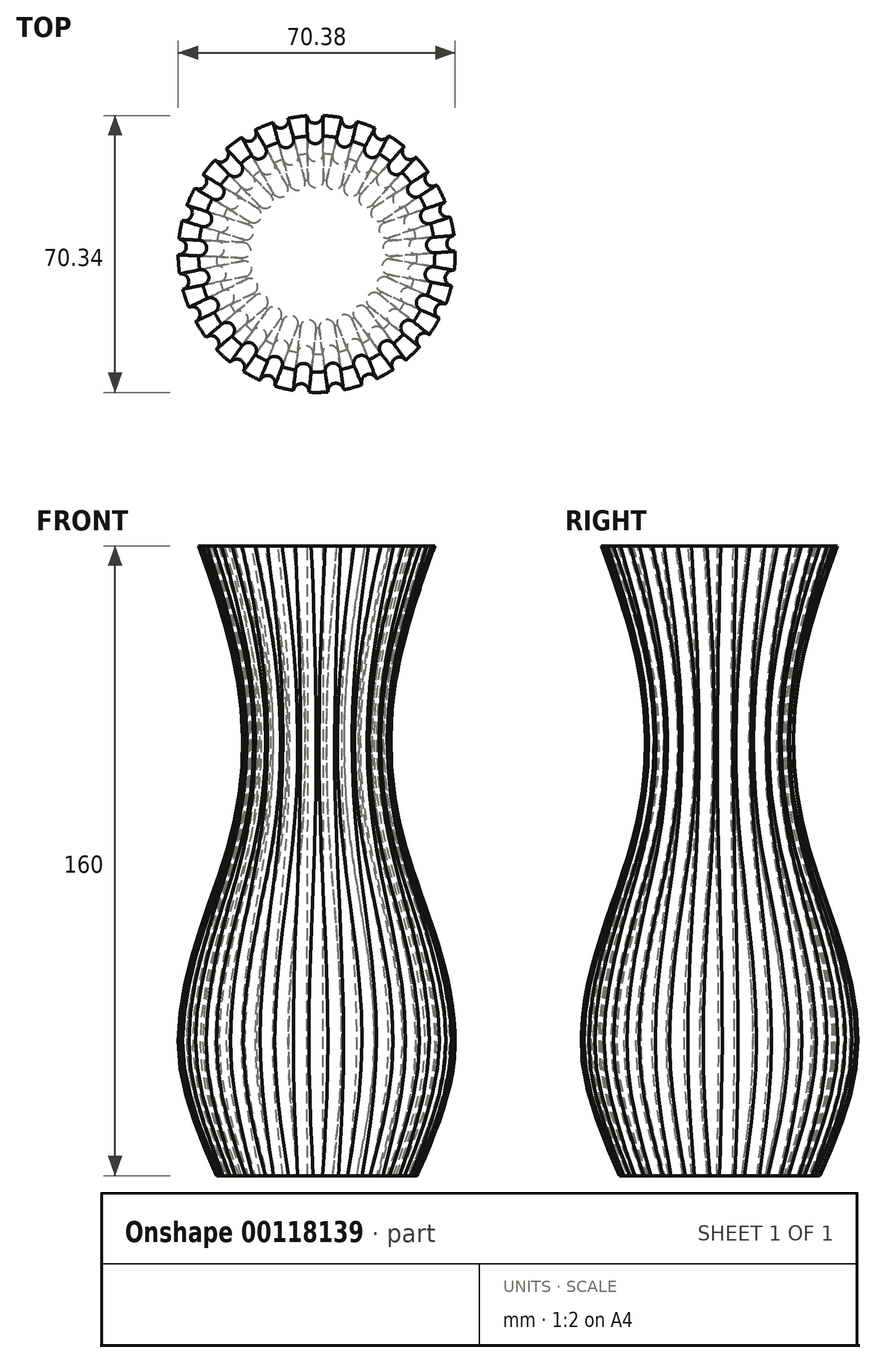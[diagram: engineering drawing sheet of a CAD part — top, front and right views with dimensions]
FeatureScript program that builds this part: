
annotation { "Feature Type Name" : "Feature", "Feature Type Description" : "" }
export const myFeature = defineFeature(function(context is Context, id is Id, definition is map)
    precondition{}
    {
        {
            var Q0;
            Q0=qCreatedBy(makeId("Top.planeOp"),FACE);
            cPlane(context, id + "F0", {"entities" : qUnion([Q0]), "cplaneType" : CPlaneType.OFFSET, "offset" : 30 * mm, "width" : 150 * mm, "height" : 150 * mm});
        }
        {
            var Q0;
            Q0=qCreatedBy(id+"F0.planeOp",FACE);
            cPlane(context, id + "F1", {"entities" : qUnion([Q0]), "cplaneType" : CPlaneType.OFFSET, "offset" : 30 * mm, "width" : 150 * mm, "height" : 150 * mm});
        }
        {
            var Q0;
            Q0=qCreatedBy(id+"F1.planeOp",FACE);
            cPlane(context, id + "F2", {"entities" : qUnion([Q0]), "cplaneType" : CPlaneType.OFFSET, "offset" : 30 * mm, "width" : 150 * mm, "height" : 150 * mm});
        }
        {
            var Q0;
            Q0=qCreatedBy(id+"F2.planeOp",FACE);
            cPlane(context, id + "F3", {"entities" : qUnion([Q0]), "cplaneType" : CPlaneType.OFFSET, "offset" : 35 * mm, "width" : 150 * mm, "height" : 150 * mm});
        }
        {
            var Q0;
            Q0=qCreatedBy(id+"F3.planeOp",FACE);
            cPlane(context, id + "F4", {"entities" : qUnion([Q0]), "cplaneType" : CPlaneType.OFFSET, "offset" : 35 * mm, "width" : 150 * mm, "height" : 150 * mm});
        }
        {
            var Q0;
            Q0=qCreatedBy(id+"F4.planeOp",FACE);
            var sketch = newSketch(context, id + "F5", { "sketchPlane" : qUnion([Q0])});
            skArc(sketch, "E0", {"start": v(-30, -0.5) * mm, "mid": v(-29.91, -2.27) * mm, "end": v(-29.73, -4.02) * mm});
            skArc(sketch, "E1", {"start": v(-29.18, 6.98) * mm, "mid": v(-26.74, 8.31) * mm, "end": v(-28, 10.8) * mm});
            skArc(sketch, "E2.1.0", {"start": v(-30, -0.5) * mm, "mid": v(-27.96, 1.4) * mm, "end": v(-29.8, 3.5) * mm});
            skArc(sketch, "E2.2.0", {"start": v(-28.93, -7.94) * mm, "mid": v(-27.43, -5.6) * mm, "end": v(-29.73, -4.02) * mm});
            skArc(sketch, "E2.3.0", {"start": v(-26.05, -14.89) * mm, "mid": v(-25.18, -12.24) * mm, "end": v(-27.8, -11.3) * mm});
            skArc(sketch, "E2.4.0", {"start": v(-21.53, -20.9) * mm, "mid": v(-21.35, -18.12) * mm, "end": v(-24.11, -17.85) * mm});
            skArc(sketch, "E2.5.0", {"start": v(-15.65, -25.6) * mm, "mid": v(-16.17, -22.86) * mm, "end": v(-18.92, -23.28) * mm});
            skArc(sketch, "E2.6.0", {"start": v(-8.8, -28.68) * mm, "mid": v(-9.97, -26.16) * mm, "end": v(-12.53, -27.26) * mm});
            skArc(sketch, "E2.7.0", {"start": v(-1.39, -29.97) * mm, "mid": v(-3.16, -27.82) * mm, "end": v(-5.36, -29.52) * mm});
            skArc(sketch, "E2.8.0", {"start": v(6.1, -29.37) * mm, "mid": v(3.86, -27.73) * mm, "end": v(2.15, -29.92) * mm});
            skArc(sketch, "E2.9.0", {"start": v(13.22, -26.93) * mm, "mid": v(10.64, -25.9) * mm, "end": v(9.52, -28.45) * mm});
            skArc(sketch, "E2.10.0", {"start": v(19.5, -22.8) * mm, "mid": v(16.75, -22.44) * mm, "end": v(16.3, -25.19) * mm});
            skArc(sketch, "E2.11.0", {"start": v(24.56, -17.23) * mm, "mid": v(21.8, -17.57) * mm, "end": v(22.05, -20.34) * mm});
            skArc(sketch, "E2.12.0", {"start": v(28.07, -10.58) * mm, "mid": v(25.49, -11.6) * mm, "end": v(26.42, -14.22) * mm});
            skArc(sketch, "E2.13.0", {"start": v(29.82, -3.27) * mm, "mid": v(27.57, -4.9) * mm, "end": v(29.12, -7.2) * mm});
            skArc(sketch, "E2.14.0", {"start": v(29.7, 4.25) * mm, "mid": v(27.92, 2.11) * mm, "end": v(30, 0.27) * mm});
            skArc(sketch, "E2.15.0", {"start": v(27.7, 11.5) * mm, "mid": v(26.52, 9) * mm, "end": v(28.99, 7.72) * mm});
            skArc(sketch, "E2.16.0", {"start": v(23.97, 18.03) * mm, "mid": v(23.45, 15.3) * mm, "end": v(26.16, 14.69) * mm});
            skArc(sketch, "E2.17.0", {"start": v(18.74, 23.43) * mm, "mid": v(18.9, 20.65) * mm, "end": v(21.69, 20.73) * mm});
            skArc(sketch, "E2.18.0", {"start": v(12.32, 27.35) * mm, "mid": v(13.18, 24.7) * mm, "end": v(15.85, 25.47) * mm});
            skArc(sketch, "E2.19.0", {"start": v(5.13, 29.56) * mm, "mid": v(6.62, 27.2) * mm, "end": v(9.02, 28.61) * mm});
            skArc(sketch, "E2.20.0", {"start": v(-2.38, 29.9) * mm, "mid": v(-0.36, 28) * mm, "end": v(1.62, 29.96) * mm});
            skArc(sketch, "E2.21.0", {"start": v(-9.74, 28.37) * mm, "mid": v(-7.3, 27.03) * mm, "end": v(-5.88, 29.42) * mm});
            skArc(sketch, "E2.22.0", {"start": v(-16.5, 25.06) * mm, "mid": v(-13.8, 24.36) * mm, "end": v(-13.01, 27.03) * mm});
            skArc(sketch, "E2.23.0", {"start": v(-22.2, 20.17) * mm, "mid": v(-19.43, 20.17) * mm, "end": v(-19.33, 22.94) * mm});
            skArc(sketch, "E2.24.0", {"start": v(-26.53, 14.01) * mm, "mid": v(-23.83, 14.7) * mm, "end": v(-24.43, 17.42) * mm});
            skArc(sketch, "E3.trimOffspring", {"start": v(-28.93, -7.94) * mm, "mid": v(-28.41, -9.63) * mm, "end": v(-27.8, -11.3) * mm});
            skArc(sketch, "E4.trimOffspring", {"start": v(-26.05, -14.89) * mm, "mid": v(-25.12, -16.4) * mm, "end": v(-24.11, -17.85) * mm});
            skArc(sketch, "E5.trimOffspring", {"start": v(-21.53, -20.9) * mm, "mid": v(-20.26, -22.13) * mm, "end": v(-18.92, -23.28) * mm});
            skArc(sketch, "E6.trimOffspring", {"start": v(-15.65, -25.6) * mm, "mid": v(-14.12, -26.47) * mm, "end": v(-12.53, -27.26) * mm});
            skArc(sketch, "E7.trimOffspring", {"start": v(-8.8, -28.68) * mm, "mid": v(-7.09, -29.15) * mm, "end": v(-5.36, -29.52) * mm});
            skArc(sketch, "E8.trimOffspring", {"start": v(-1.39, -29.97) * mm, "mid": v(0.38, -30) * mm, "end": v(2.15, -29.92) * mm});
            skArc(sketch, "E9.trimOffspring", {"start": v(6.1, -29.37) * mm, "mid": v(7.83, -28.96) * mm, "end": v(9.52, -28.45) * mm});
            skArc(sketch, "E10.trimOffspring", {"start": v(13.22, -26.93) * mm, "mid": v(14.79, -26.1) * mm, "end": v(16.3, -25.19) * mm});
            skArc(sketch, "E11.trimOffspring", {"start": v(19.5, -22.8) * mm, "mid": v(20.81, -21.6) * mm, "end": v(22.05, -20.34) * mm});
            skArc(sketch, "E12.trimOffspring", {"start": v(24.56, -17.23) * mm, "mid": v(25.53, -15.75) * mm, "end": v(26.42, -14.22) * mm});
            skArc(sketch, "E13.trimOffspring", {"start": v(28.07, -10.58) * mm, "mid": v(28.65, -8.9) * mm, "end": v(29.12, -7.2) * mm});
            skArc(sketch, "E14.trimOffspring", {"start": v(29.82, -3.27) * mm, "mid": v(29.96, -1.5) * mm, "end": v(30, 0.27) * mm});
            skArc(sketch, "E15.trimOffspring", {"start": v(29.7, 4.25) * mm, "mid": v(29.4, 6) * mm, "end": v(28.99, 7.72) * mm});
            skArc(sketch, "E16.trimOffspring", {"start": v(27.7, 11.5) * mm, "mid": v(26.98, 13.12) * mm, "end": v(26.16, 14.69) * mm});
            skArc(sketch, "E17.trimOffspring", {"start": v(23.97, 18.03) * mm, "mid": v(22.87, 19.42) * mm, "end": v(21.69, 20.73) * mm});
            skArc(sketch, "E18.trimOffspring", {"start": v(18.74, 23.43) * mm, "mid": v(17.32, 24.5) * mm, "end": v(15.85, 25.47) * mm});
            skArc(sketch, "E19.trimOffspring", {"start": v(12.32, 27.35) * mm, "mid": v(10.69, 28.03) * mm, "end": v(9.02, 28.61) * mm});
            skArc(sketch, "E20.trimOffspring", {"start": v(5.13, 29.56) * mm, "mid": v(3.38, 29.8) * mm, "end": v(1.62, 29.96) * mm});
            skArc(sketch, "E21.trimOffspring", {"start": v(-2.38, 29.9) * mm, "mid": v(-4.14, 29.71) * mm, "end": v(-5.88, 29.42) * mm});
            skArc(sketch, "E22.trimOffspring", {"start": v(-9.74, 28.37) * mm, "mid": v(-11.4, 27.75) * mm, "end": v(-13.01, 27.03) * mm});
            skArc(sketch, "E23.trimOffspring", {"start": v(-16.5, 25.06) * mm, "mid": v(-17.94, 24.04) * mm, "end": v(-19.33, 22.94) * mm});
            skArc(sketch, "E24.trimOffspring", {"start": v(-22.2, 20.17) * mm, "mid": v(-23.36, 18.83) * mm, "end": v(-24.43, 17.42) * mm});
            skArc(sketch, "E25.trimOffspring", {"start": v(-26.53, 14.01) * mm, "mid": v(-27.3, 12.43) * mm, "end": v(-28, 10.8) * mm});
            skArc(sketch, "E26.trimOffspring", {"start": v(-29.18, 6.98) * mm, "mid": v(-29.54, 5.25) * mm, "end": v(-29.8, 3.5) * mm});
            skSolve(sketch);
        }
        {
            var Q0;
            Q0=qCreatedBy(id+"F3.planeOp",FACE);
            var sketch = newSketch(context, id + "F6", { "sketchPlane" : qUnion([Q0])});
            skArc(sketch, "E27", {"start": v(-19.98, -1) * mm, "mid": v(-19.94, -1.51) * mm, "end": v(-19.9, -2.02) * mm});
            skArc(sketch, "E28", {"start": v(-19.6, 4) * mm, "mid": v(-17.19, 5.34) * mm, "end": v(-18.4, 7.82) * mm});
            skArc(sketch, "E29.1.0", {"start": v(-19.98, -1) * mm, "mid": v(-17.98, 0.9) * mm, "end": v(-19.78, 3) * mm});
            skArc(sketch, "E29.2.0", {"start": v(-19.1, -5.93) * mm, "mid": v(-17.64, -3.6) * mm, "end": v(-19.9, -2.02) * mm});
            skArc(sketch, "E29.3.0", {"start": v(-17.02, -10.5) * mm, "mid": v(-16.19, -7.87) * mm, "end": v(-18.77, -6.9) * mm});
            skArc(sketch, "E29.4.0", {"start": v(-13.88, -14.4) * mm, "mid": v(-13.72, -11.65) * mm, "end": v(-16.46, -11.36) * mm});
            skArc(sketch, "E29.5.0", {"start": v(-9.86, -17.4) * mm, "mid": v(-10.4, -14.7) * mm, "end": v(-13.12, -15.1) * mm});
            skArc(sketch, "E29.6.0", {"start": v(-5.22, -19.3) * mm, "mid": v(-6.41, -16.82) * mm, "end": v(-8.96, -17.88) * mm});
            skArc(sketch, "E29.7.0", {"start": v(-0.26, -20) * mm, "mid": v(-2.03, -17.89) * mm, "end": v(-4.23, -19.55) * mm});
            skArc(sketch, "E29.8.0", {"start": v(4.72, -19.43) * mm, "mid": v(2.48, -17.83) * mm, "end": v(0.77, -19.99) * mm});
            skArc(sketch, "E29.9.0", {"start": v(9.4, -17.65) * mm, "mid": v(6.84, -16.65) * mm, "end": v(5.71, -19.17) * mm});
            skArc(sketch, "E29.10.0", {"start": v(13.5, -14.75) * mm, "mid": v(10.76, -14.43) * mm, "end": v(10.3, -17.14) * mm});
            skArc(sketch, "E29.11.0", {"start": v(16.75, -10.93) * mm, "mid": v(14.01, -11.3) * mm, "end": v(14.24, -14.04) * mm});
            skArc(sketch, "E29.12.0", {"start": v(18.94, -6.42) * mm, "mid": v(16.38, -7.46) * mm, "end": v(17.29, -10.06) * mm});
            skArc(sketch, "E29.13.0", {"start": v(19.94, -1.51) * mm, "mid": v(17.72, -3.15) * mm, "end": v(19.24, -5.45) * mm});
            skArc(sketch, "E29.14.0", {"start": v(19.7, 3.5) * mm, "mid": v(17.95, 1.36) * mm, "end": v(20, -0.49) * mm});
            skArc(sketch, "E29.15.0", {"start": v(18.2, 8.28) * mm, "mid": v(17.05, 5.78) * mm, "end": v(19.49, 4.5) * mm});
            skArc(sketch, "E29.16.0", {"start": v(15.57, 12.55) * mm, "mid": v(15.07, 9.84) * mm, "end": v(17.76, 9.2) * mm});
            skArc(sketch, "E29.17.0", {"start": v(11.96, 16.03) * mm, "mid": v(12.15, 13.28) * mm, "end": v(14.9, 13.33) * mm});
            skArc(sketch, "E29.18.0", {"start": v(7.6, 18.5) * mm, "mid": v(8.47, 15.88) * mm, "end": v(11.13, 16.62) * mm});
            skArc(sketch, "E29.19.0", {"start": v(2.76, 19.8) * mm, "mid": v(4.25, 17.5) * mm, "end": v(6.64, 18.86) * mm});
            skArc(sketch, "E29.20.0", {"start": v(-2.25, 19.87) * mm, "mid": v(-0.23, 18) * mm, "end": v(1.74, 19.92) * mm});
            skArc(sketch, "E29.21.0", {"start": v(-7.12, 18.69) * mm, "mid": v(-4.7, 17.38) * mm, "end": v(-3.27, 19.73) * mm});
            skArc(sketch, "E29.22.0", {"start": v(-11.55, 16.33) * mm, "mid": v(-8.87, 15.66) * mm, "end": v(-8.07, 18.3) * mm});
            skArc(sketch, "E29.23.0", {"start": v(-15.24, 12.95) * mm, "mid": v(-12.49, 12.96) * mm, "end": v(-12.37, 15.72) * mm});
            skArc(sketch, "E29.24.0", {"start": v(-17.99, 8.75) * mm, "mid": v(-15.32, 9.45) * mm, "end": v(-15.89, 12.15) * mm});
            skArc(sketch, "E30.trimOffspring", {"start": v(-19.1, -5.93) * mm, "mid": v(-18.94, -6.42) * mm, "end": v(-18.77, -6.9) * mm});
            skArc(sketch, "E31.trimOffspring", {"start": v(-17.02, -10.5) * mm, "mid": v(-16.75, -10.93) * mm, "end": v(-16.46, -11.36) * mm});
            skArc(sketch, "E32.trimOffspring", {"start": v(-13.88, -14.4) * mm, "mid": v(-13.5, -14.75) * mm, "end": v(-13.12, -15.1) * mm});
            skArc(sketch, "E33.trimOffspring", {"start": v(-9.86, -17.4) * mm, "mid": v(-9.41, -17.65) * mm, "end": v(-8.96, -17.88) * mm});
            skArc(sketch, "E34.trimOffspring", {"start": v(-5.22, -19.3) * mm, "mid": v(-4.73, -19.43) * mm, "end": v(-4.23, -19.55) * mm});
            skArc(sketch, "E35.trimOffspring", {"start": v(-0.26, -20) * mm, "mid": v(0.25, -20) * mm, "end": v(0.77, -19.99) * mm});
            skArc(sketch, "E36.trimOffspring", {"start": v(4.72, -19.43) * mm, "mid": v(5.22, -19.3) * mm, "end": v(5.71, -19.17) * mm});
            skArc(sketch, "E37.trimOffspring", {"start": v(9.4, -17.65) * mm, "mid": v(9.86, -17.4) * mm, "end": v(10.3, -17.14) * mm});
            skArc(sketch, "E38.trimOffspring", {"start": v(13.5, -14.75) * mm, "mid": v(13.88, -14.4) * mm, "end": v(14.24, -14.04) * mm});
            skArc(sketch, "E39.trimOffspring", {"start": v(16.75, -10.93) * mm, "mid": v(17.02, -10.5) * mm, "end": v(17.29, -10.06) * mm});
            skArc(sketch, "E40.trimOffspring", {"start": v(18.94, -6.42) * mm, "mid": v(19.1, -5.94) * mm, "end": v(19.24, -5.45) * mm});
            skArc(sketch, "E41.trimOffspring", {"start": v(19.94, -1.51) * mm, "mid": v(19.97, -1) * mm, "end": v(20, -0.49) * mm});
            skArc(sketch, "E42.trimOffspring", {"start": v(19.7, 3.5) * mm, "mid": v(19.6, 4) * mm, "end": v(19.49, 4.5) * mm});
            skArc(sketch, "E43.trimOffspring", {"start": v(18.2, 8.28) * mm, "mid": v(17.99, 8.75) * mm, "end": v(17.76, 9.2) * mm});
            skArc(sketch, "E44.trimOffspring", {"start": v(15.57, 12.55) * mm, "mid": v(15.25, 12.94) * mm, "end": v(14.9, 13.33) * mm});
            skArc(sketch, "E45.trimOffspring", {"start": v(11.96, 16.03) * mm, "mid": v(11.55, 16.33) * mm, "end": v(11.13, 16.62) * mm});
            skArc(sketch, "E46.trimOffspring", {"start": v(7.6, 18.5) * mm, "mid": v(7.12, 18.69) * mm, "end": v(6.64, 18.86) * mm});
            skArc(sketch, "E47.trimOffspring", {"start": v(2.76, 19.8) * mm, "mid": v(2.25, 19.87) * mm, "end": v(1.74, 19.92) * mm});
            skArc(sketch, "E48.trimOffspring", {"start": v(-2.25, 19.87) * mm, "mid": v(-2.76, 19.8) * mm, "end": v(-3.27, 19.73) * mm});
            skArc(sketch, "E49.trimOffspring", {"start": v(-7.12, 18.69) * mm, "mid": v(-7.6, 18.5) * mm, "end": v(-8.07, 18.3) * mm});
            skArc(sketch, "E50.trimOffspring", {"start": v(-11.55, 16.33) * mm, "mid": v(-11.96, 16.03) * mm, "end": v(-12.37, 15.72) * mm});
            skArc(sketch, "E51.trimOffspring", {"start": v(-15.24, 12.95) * mm, "mid": v(-15.57, 12.55) * mm, "end": v(-15.89, 12.15) * mm});
            skArc(sketch, "E52.trimOffspring", {"start": v(-17.99, 8.75) * mm, "mid": v(-18.2, 8.28) * mm, "end": v(-18.4, 7.82) * mm});
            skArc(sketch, "E53.trimOffspring", {"start": v(-19.6, 4) * mm, "mid": v(-19.7, 3.5) * mm, "end": v(-19.78, 3) * mm});
            skSolve(sketch);
        }
        {
            var Q0;
            Q0=qCreatedBy(id+"F2.planeOp",FACE);
            var sketch = newSketch(context, id + "F7", { "sketchPlane" : qUnion([Q0])});
            skArc(sketch, "E54", {"start": v(-20.98, -0.95) * mm, "mid": v(-20.94, -1.59) * mm, "end": v(-20.88, -2.22) * mm});
            skArc(sketch, "E55", {"start": v(-20.56, 4.3) * mm, "mid": v(-18.14, 5.64) * mm, "end": v(-19.37, 8.11) * mm});
            skArc(sketch, "E56.1.0", {"start": v(-20.98, -0.95) * mm, "mid": v(-18.98, 0.95) * mm, "end": v(-20.78, 3.04) * mm});
            skArc(sketch, "E56.2.0", {"start": v(-20.08, -6.14) * mm, "mid": v(-18.62, -3.8) * mm, "end": v(-20.88, -2.22) * mm});
            skArc(sketch, "E56.3.0", {"start": v(-17.93, -10.94) * mm, "mid": v(-17.09, -8.3) * mm, "end": v(-19.67, -7.34) * mm});
            skArc(sketch, "E56.4.0", {"start": v(-14.64, -15.05) * mm, "mid": v(-14.48, -12.3) * mm, "end": v(-17.23, -12) * mm});
            skArc(sketch, "E56.5.0", {"start": v(-10.44, -18.22) * mm, "mid": v(-10.97, -15.51) * mm, "end": v(-13.7, -15.91) * mm});
            skArc(sketch, "E56.6.0", {"start": v(-5.58, -20.24) * mm, "mid": v(-6.77, -17.75) * mm, "end": v(-9.31, -18.82) * mm});
            skArc(sketch, "E56.7.0", {"start": v(-0.37, -21) * mm, "mid": v(-2.14, -18.88) * mm, "end": v(-4.34, -20.55) * mm});
            skArc(sketch, "E56.8.0", {"start": v(4.86, -20.43) * mm, "mid": v(2.62, -18.82) * mm, "end": v(0.9, -20.98) * mm});
            skArc(sketch, "E56.9.0", {"start": v(9.8, -18.58) * mm, "mid": v(7.22, -17.58) * mm, "end": v(6.1, -20.1) * mm});
            skArc(sketch, "E56.10.0", {"start": v(14.1, -15.56) * mm, "mid": v(11.36, -15.23) * mm, "end": v(10.9, -17.95) * mm});
            skArc(sketch, "E56.11.0", {"start": v(17.53, -11.56) * mm, "mid": v(14.8, -11.92) * mm, "end": v(15.02, -14.67) * mm});
            skArc(sketch, "E56.12.0", {"start": v(19.85, -6.84) * mm, "mid": v(17.3, -7.87) * mm, "end": v(18.2, -10.48) * mm});
            skArc(sketch, "E56.13.0", {"start": v(20.93, -1.69) * mm, "mid": v(18.7, -3.32) * mm, "end": v(20.23, -5.62) * mm});
            skArc(sketch, "E56.14.0", {"start": v(20.7, 3.57) * mm, "mid": v(18.95, 1.43) * mm, "end": v(21, -0.41) * mm});
            skArc(sketch, "E56.15.0", {"start": v(19.16, 8.6) * mm, "mid": v(18, 6.1) * mm, "end": v(20.44, 4.82) * mm});
            skArc(sketch, "E56.16.0", {"start": v(16.41, 13.1) * mm, "mid": v(15.91, 10.38) * mm, "end": v(18.6, 9.75) * mm});
            skArc(sketch, "E56.17.0", {"start": v(12.64, 16.77) * mm, "mid": v(12.83, 14.02) * mm, "end": v(15.59, 14.07) * mm});
            skArc(sketch, "E56.18.0", {"start": v(8.07, 19.39) * mm, "mid": v(8.94, 16.77) * mm, "end": v(11.6, 17.5) * mm});
            skArc(sketch, "E56.19.0", {"start": v(3, 20.78) * mm, "mid": v(4.5, 18.46) * mm, "end": v(6.88, 19.84) * mm});
            skArc(sketch, "E56.20.0", {"start": v(-2.26, 20.88) * mm, "mid": v(-0.24, 19) * mm, "end": v(1.73, 20.93) * mm});
            skArc(sketch, "E56.21.0", {"start": v(-7.38, 19.66) * mm, "mid": v(-4.96, 18.34) * mm, "end": v(-3.53, 20.7) * mm});
            skArc(sketch, "E56.22.0", {"start": v(-12.04, 17.2) * mm, "mid": v(-9.36, 16.53) * mm, "end": v(-8.57, 19.17) * mm});
            skArc(sketch, "E56.23.0", {"start": v(-15.94, 13.67) * mm, "mid": v(-13.18, 13.68) * mm, "end": v(-13.06, 16.44) * mm});
            skArc(sketch, "E56.24.0", {"start": v(-18.84, 9.28) * mm, "mid": v(-16.17, 9.98) * mm, "end": v(-16.74, 12.68) * mm});
            skArc(sketch, "E57.trimOffspring", {"start": v(-20.08, -6.14) * mm, "mid": v(-19.89, -6.74) * mm, "end": v(-19.67, -7.34) * mm});
            skArc(sketch, "E58.trimOffspring", {"start": v(-17.93, -10.94) * mm, "mid": v(-17.59, -11.48) * mm, "end": v(-17.23, -12) * mm});
            skArc(sketch, "E59.trimOffspring", {"start": v(-14.64, -15.05) * mm, "mid": v(-14.18, -15.5) * mm, "end": v(-13.7, -15.91) * mm});
            skArc(sketch, "E60.trimOffspring", {"start": v(-10.44, -18.22) * mm, "mid": v(-9.88, -18.53) * mm, "end": v(-9.31, -18.82) * mm});
            skArc(sketch, "E61.trimOffspring", {"start": v(-5.58, -20.24) * mm, "mid": v(-4.96, -20.4) * mm, "end": v(-4.34, -20.55) * mm});
            skArc(sketch, "E62.trimOffspring", {"start": v(-0.37, -21) * mm, "mid": v(0.27, -21) * mm, "end": v(0.9, -20.98) * mm});
            skArc(sketch, "E63.trimOffspring", {"start": v(4.86, -20.43) * mm, "mid": v(5.48, -20.27) * mm, "end": v(6.1, -20.1) * mm});
            skArc(sketch, "E64.trimOffspring", {"start": v(9.8, -18.58) * mm, "mid": v(10.35, -18.27) * mm, "end": v(10.9, -17.95) * mm});
            skArc(sketch, "E65.trimOffspring", {"start": v(14.1, -15.56) * mm, "mid": v(14.57, -15.12) * mm, "end": v(15.02, -14.67) * mm});
            skArc(sketch, "E66.trimOffspring", {"start": v(17.53, -11.56) * mm, "mid": v(17.87, -11.03) * mm, "end": v(18.2, -10.48) * mm});
            skArc(sketch, "E67.trimOffspring", {"start": v(19.85, -6.84) * mm, "mid": v(20.05, -6.23) * mm, "end": v(20.23, -5.62) * mm});
            skArc(sketch, "E68.trimOffspring", {"start": v(20.93, -1.69) * mm, "mid": v(20.97, -1.05) * mm, "end": v(21, -0.41) * mm});
            skArc(sketch, "E69.trimOffspring", {"start": v(20.7, 3.57) * mm, "mid": v(20.58, 4.2) * mm, "end": v(20.44, 4.82) * mm});
            skArc(sketch, "E70.trimOffspring", {"start": v(19.16, 8.6) * mm, "mid": v(18.89, 9.18) * mm, "end": v(18.6, 9.75) * mm});
            skArc(sketch, "E71.trimOffspring", {"start": v(16.41, 13.1) * mm, "mid": v(16, 13.6) * mm, "end": v(15.59, 14.07) * mm});
            skArc(sketch, "E72.trimOffspring", {"start": v(12.64, 16.77) * mm, "mid": v(12.13, 17.15) * mm, "end": v(11.6, 17.5) * mm});
            skArc(sketch, "E73.trimOffspring", {"start": v(8.07, 19.39) * mm, "mid": v(7.48, 19.62) * mm, "end": v(6.88, 19.84) * mm});
            skArc(sketch, "E74.trimOffspring", {"start": v(3, 20.78) * mm, "mid": v(2.37, 20.87) * mm, "end": v(1.73, 20.93) * mm});
            skArc(sketch, "E75.trimOffspring", {"start": v(-2.26, 20.88) * mm, "mid": v(-2.9, 20.8) * mm, "end": v(-3.53, 20.7) * mm});
            skArc(sketch, "E76.trimOffspring", {"start": v(-7.38, 19.66) * mm, "mid": v(-7.98, 19.43) * mm, "end": v(-8.57, 19.17) * mm});
            skArc(sketch, "E77.trimOffspring", {"start": v(-12.04, 17.2) * mm, "mid": v(-12.56, 16.83) * mm, "end": v(-13.06, 16.44) * mm});
            skArc(sketch, "E78.trimOffspring", {"start": v(-15.94, 13.67) * mm, "mid": v(-16.35, 13.18) * mm, "end": v(-16.74, 12.68) * mm});
            skArc(sketch, "E79.trimOffspring", {"start": v(-18.84, 9.28) * mm, "mid": v(-19.11, 8.7) * mm, "end": v(-19.37, 8.11) * mm});
            skArc(sketch, "E80.trimOffspring", {"start": v(-20.56, 4.3) * mm, "mid": v(-20.68, 3.67) * mm, "end": v(-20.78, 3.04) * mm});
            skSolve(sketch);
        }
        {
            var Q0;
            Q0=qCreatedBy(id+"F1.planeOp",FACE);
            var sketch = newSketch(context, id + "F8", { "sketchPlane" : qUnion([Q0])});
            skArc(sketch, "E81", {"start": v(-30.5, -0.47) * mm, "mid": v(-30.41, -2.3) * mm, "end": v(-30.22, -4.12) * mm});
            skArc(sketch, "E82", {"start": v(-29.66, 7.13) * mm, "mid": v(-27.22, 8.46) * mm, "end": v(-28.47, 10.94) * mm});
            skArc(sketch, "E83.1.0", {"start": v(-30.5, -0.47) * mm, "mid": v(-28.46, 1.43) * mm, "end": v(-30.3, 3.52) * mm});
            skArc(sketch, "E83.2.0", {"start": v(-29.42, -8.04) * mm, "mid": v(-27.92, -5.7) * mm, "end": v(-30.22, -4.12) * mm});
            skArc(sketch, "E83.3.0", {"start": v(-26.5, -15.1) * mm, "mid": v(-25.63, -12.46) * mm, "end": v(-28.24, -11.51) * mm});
            skArc(sketch, "E83.4.0", {"start": v(-21.9, -21.22) * mm, "mid": v(-21.73, -18.44) * mm, "end": v(-24.5, -18.17) * mm});
            skArc(sketch, "E83.5.0", {"start": v(-15.94, -26) * mm, "mid": v(-16.46, -23.27) * mm, "end": v(-19.2, -23.7) * mm});
            skArc(sketch, "E83.6.0", {"start": v(-8.97, -29.15) * mm, "mid": v(-10.15, -26.63) * mm, "end": v(-12.7, -27.73) * mm});
            skArc(sketch, "E83.7.0", {"start": v(-1.44, -30.47) * mm, "mid": v(-3.21, -28.32) * mm, "end": v(-5.42, -30.02) * mm});
            skArc(sketch, "E83.8.0", {"start": v(6.18, -29.87) * mm, "mid": v(3.93, -28.23) * mm, "end": v(2.22, -30.42) * mm});
            skArc(sketch, "E83.9.0", {"start": v(13.41, -27.4) * mm, "mid": v(10.83, -26.36) * mm, "end": v(9.71, -28.91) * mm});
            skArc(sketch, "E83.10.0", {"start": v(19.8, -23.2) * mm, "mid": v(17.04, -22.84) * mm, "end": v(16.6, -25.59) * mm});
            skArc(sketch, "E83.11.0", {"start": v(24.95, -17.54) * mm, "mid": v(22.19, -17.89) * mm, "end": v(22.44, -20.66) * mm});
            skArc(sketch, "E83.12.0", {"start": v(28.53, -10.79) * mm, "mid": v(25.94, -11.8) * mm, "end": v(26.87, -14.43) * mm});
            skArc(sketch, "E83.13.0", {"start": v(30.32, -3.35) * mm, "mid": v(28.06, -4.98) * mm, "end": v(29.62, -7.29) * mm});
            skArc(sketch, "E83.14.0", {"start": v(30.2, 4.3) * mm, "mid": v(28.42, 2.15) * mm, "end": v(30.5, 0.3) * mm});
            skArc(sketch, "E83.15.0", {"start": v(28.18, 11.67) * mm, "mid": v(27, 9.15) * mm, "end": v(29.46, 7.88) * mm});
            skArc(sketch, "E83.16.0", {"start": v(24.4, 18.3) * mm, "mid": v(23.87, 15.58) * mm, "end": v(26.58, 14.96) * mm});
            skArc(sketch, "E83.17.0", {"start": v(19.07, 23.8) * mm, "mid": v(19.24, 21.02) * mm, "end": v(22.02, 21.1) * mm});
            skArc(sketch, "E83.18.0", {"start": v(12.56, 27.8) * mm, "mid": v(13.41, 25.15) * mm, "end": v(16.08, 25.91) * mm});
            skArc(sketch, "E83.19.0", {"start": v(5.25, 30.04) * mm, "mid": v(6.74, 27.7) * mm, "end": v(9.13, 29.1) * mm});
            skArc(sketch, "E83.20.0", {"start": v(-2.39, 30.4) * mm, "mid": v(-0.36, 28.5) * mm, "end": v(1.61, 30.46) * mm});
            skArc(sketch, "E83.21.0", {"start": v(-9.87, 28.86) * mm, "mid": v(-7.44, 27.51) * mm, "end": v(-6.01, 29.9) * mm});
            skArc(sketch, "E83.22.0", {"start": v(-16.74, 25.5) * mm, "mid": v(-14.05, 24.8) * mm, "end": v(-13.26, 27.47) * mm});
            skArc(sketch, "E83.23.0", {"start": v(-22.55, 20.53) * mm, "mid": v(-19.77, 20.53) * mm, "end": v(-19.68, 23.3) * mm});
            skArc(sketch, "E83.24.0", {"start": v(-26.95, 14.28) * mm, "mid": v(-24.26, 14.96) * mm, "end": v(-24.85, 17.68) * mm});
            skArc(sketch, "E84.trimOffspring", {"start": v(-29.42, -8.04) * mm, "mid": v(-28.88, -9.8) * mm, "end": v(-28.24, -11.51) * mm});
            skArc(sketch, "E85.trimOffspring", {"start": v(-26.5, -15.1) * mm, "mid": v(-25.54, -16.67) * mm, "end": v(-24.5, -18.17) * mm});
            skArc(sketch, "E86.trimOffspring", {"start": v(-21.9, -21.22) * mm, "mid": v(-20.6, -22.5) * mm, "end": v(-19.2, -23.7) * mm});
            skArc(sketch, "E87.trimOffspring", {"start": v(-15.94, -26) * mm, "mid": v(-14.35, -26.91) * mm, "end": v(-12.7, -27.73) * mm});
            skArc(sketch, "E88.trimOffspring", {"start": v(-8.97, -29.15) * mm, "mid": v(-7.2, -29.64) * mm, "end": v(-5.42, -30.02) * mm});
            skArc(sketch, "E89.trimOffspring", {"start": v(-1.44, -30.47) * mm, "mid": v(0.39, -30.5) * mm, "end": v(2.22, -30.42) * mm});
            skArc(sketch, "E90.trimOffspring", {"start": v(6.18, -29.87) * mm, "mid": v(7.96, -29.44) * mm, "end": v(9.71, -28.91) * mm});
            skArc(sketch, "E91.trimOffspring", {"start": v(13.41, -27.4) * mm, "mid": v(15.03, -26.54) * mm, "end": v(16.6, -25.59) * mm});
            skArc(sketch, "E92.trimOffspring", {"start": v(19.8, -23.2) * mm, "mid": v(21.16, -21.97) * mm, "end": v(22.44, -20.66) * mm});
            skArc(sketch, "E93.trimOffspring", {"start": v(24.95, -17.54) * mm, "mid": v(25.96, -16.01) * mm, "end": v(26.87, -14.43) * mm});
            skArc(sketch, "E94.trimOffspring", {"start": v(28.53, -10.79) * mm, "mid": v(29.12, -9.05) * mm, "end": v(29.62, -7.29) * mm});
            skArc(sketch, "E95.trimOffspring", {"start": v(30.32, -3.35) * mm, "mid": v(30.46, -1.53) * mm, "end": v(30.5, 0.3) * mm});
            skArc(sketch, "E96.trimOffspring", {"start": v(30.2, 4.3) * mm, "mid": v(29.88, 6.1) * mm, "end": v(29.46, 7.88) * mm});
            skArc(sketch, "E97.trimOffspring", {"start": v(28.18, 11.67) * mm, "mid": v(27.43, 13.34) * mm, "end": v(26.58, 14.96) * mm});
            skArc(sketch, "E98.trimOffspring", {"start": v(24.4, 18.3) * mm, "mid": v(23.25, 19.74) * mm, "end": v(22.02, 21.1) * mm});
            skArc(sketch, "E99.trimOffspring", {"start": v(19.07, 23.8) * mm, "mid": v(17.61, 24.9) * mm, "end": v(16.08, 25.91) * mm});
            skArc(sketch, "E100.trimOffspring", {"start": v(12.56, 27.8) * mm, "mid": v(10.87, 28.5) * mm, "end": v(9.13, 29.1) * mm});
            skArc(sketch, "E101.trimOffspring", {"start": v(5.25, 30.04) * mm, "mid": v(3.44, 30.3) * mm, "end": v(1.61, 30.46) * mm});
            skArc(sketch, "E102.trimOffspring", {"start": v(-2.39, 30.4) * mm, "mid": v(-4.2, 30.2) * mm, "end": v(-6.01, 29.9) * mm});
            skArc(sketch, "E103.trimOffspring", {"start": v(-9.87, 28.86) * mm, "mid": v(-11.59, 28.21) * mm, "end": v(-13.26, 27.47) * mm});
            skArc(sketch, "E104.trimOffspring", {"start": v(-16.74, 25.5) * mm, "mid": v(-18.24, 24.44) * mm, "end": v(-19.68, 23.3) * mm});
            skArc(sketch, "E105.trimOffspring", {"start": v(-22.55, 20.53) * mm, "mid": v(-23.75, 19.14) * mm, "end": v(-24.85, 17.68) * mm});
            skArc(sketch, "E106.trimOffspring", {"start": v(-26.95, 14.28) * mm, "mid": v(-27.76, 12.63) * mm, "end": v(-28.47, 10.94) * mm});
            skArc(sketch, "E107.trimOffspring", {"start": v(-29.66, 7.13) * mm, "mid": v(-30.03, 5.33) * mm, "end": v(-30.3, 3.52) * mm});
            skSolve(sketch);
        }
        {
            var Q0;
            Q0=qCreatedBy(id+"F0.planeOp",FACE);
            var sketch = newSketch(context, id + "F9", { "sketchPlane" : qUnion([Q0])});
            skArc(sketch, "E108", {"start": v(-35, -0.25) * mm, "mid": v(-34.9, -2.64) * mm, "end": v(-34.64, -5.03) * mm});
            skArc(sketch, "E109", {"start": v(-33.96, 8.46) * mm, "mid": v(-31.51, 9.8) * mm, "end": v(-32.77, 12.28) * mm});
            skArc(sketch, "E110.1.0", {"start": v(-35, -0.25) * mm, "mid": v(-32.96, 1.65) * mm, "end": v(-34.8, 3.75) * mm});
            skArc(sketch, "E110.2.0", {"start": v(-33.84, -8.94) * mm, "mid": v(-32.33, -6.6) * mm, "end": v(-34.64, -5.03) * mm});
            skArc(sketch, "E110.3.0", {"start": v(-30.55, -17.08) * mm, "mid": v(-29.68, -14.43) * mm, "end": v(-32.3, -13.48) * mm});
            skArc(sketch, "E110.4.0", {"start": v(-25.34, -24.14) * mm, "mid": v(-25.16, -21.36) * mm, "end": v(-27.93, -21.1) * mm});
            skArc(sketch, "E110.5.0", {"start": v(-18.54, -29.68) * mm, "mid": v(-19.06, -26.94) * mm, "end": v(-21.8, -27.37) * mm});
            skArc(sketch, "E110.6.0", {"start": v(-10.58, -33.36) * mm, "mid": v(-11.76, -30.83) * mm, "end": v(-14.32, -31.94) * mm});
            skArc(sketch, "E110.7.0", {"start": v(-1.95, -34.95) * mm, "mid": v(-3.72, -32.79) * mm, "end": v(-5.92, -34.5) * mm});
            skArc(sketch, "E110.8.0", {"start": v(6.8, -34.33) * mm, "mid": v(4.55, -32.68) * mm, "end": v(2.84, -34.88) * mm});
            skArc(sketch, "E110.9.0", {"start": v(15.13, -31.56) * mm, "mid": v(12.54, -30.53) * mm, "end": v(11.43, -33.08) * mm});
            skArc(sketch, "E110.10.0", {"start": v(22.5, -26.8) * mm, "mid": v(19.74, -26.45) * mm, "end": v(19.3, -29.2) * mm});
            skArc(sketch, "E110.11.0", {"start": v(28.46, -20.37) * mm, "mid": v(25.7, -20.7) * mm, "end": v(25.95, -23.49) * mm});
            skArc(sketch, "E110.12.0", {"start": v(32.63, -12.65) * mm, "mid": v(30.04, -13.67) * mm, "end": v(30.98, -16.3) * mm});
            skArc(sketch, "E110.13.0", {"start": v(34.75, -4.14) * mm, "mid": v(32.5, -5.77) * mm, "end": v(34.06, -8.08) * mm});
            skArc(sketch, "E110.14.0", {"start": v(34.7, 4.63) * mm, "mid": v(32.9, 2.5) * mm, "end": v(35, 0.64) * mm});
            skArc(sketch, "E110.15.0", {"start": v(32.45, 13.11) * mm, "mid": v(31.25, 10.6) * mm, "end": v(33.73, 9.33) * mm});
            skArc(sketch, "E110.16.0", {"start": v(28.17, 20.77) * mm, "mid": v(27.64, 18.04) * mm, "end": v(30.35, 17.42) * mm});
            skArc(sketch, "E110.17.0", {"start": v(22.12, 27.12) * mm, "mid": v(22.28, 24.34) * mm, "end": v(25.07, 24.43) * mm});
            skArc(sketch, "E110.18.0", {"start": v(14.68, 31.77) * mm, "mid": v(15.53, 29.12) * mm, "end": v(18.2, 29.9) * mm});
            skArc(sketch, "E110.19.0", {"start": v(6.32, 34.43) * mm, "mid": v(7.8, 32.07) * mm, "end": v(10.2, 33.48) * mm});
            skArc(sketch, "E110.20.0", {"start": v(-2.44, 34.91) * mm, "mid": v(-0.42, 33) * mm, "end": v(1.55, 34.97) * mm});
            skArc(sketch, "E110.21.0", {"start": v(-11.05, 33.2) * mm, "mid": v(-8.61, 31.86) * mm, "end": v(-7.2, 34.25) * mm});
            skArc(sketch, "E110.22.0", {"start": v(-18.96, 29.42) * mm, "mid": v(-16.27, 28.71) * mm, "end": v(-15.48, 31.39) * mm});
            skArc(sketch, "E110.23.0", {"start": v(-25.68, 23.78) * mm, "mid": v(-22.9, 23.77) * mm, "end": v(-22.8, 26.55) * mm});
            skArc(sketch, "E110.24.0", {"start": v(-30.79, 16.64) * mm, "mid": v(-28.09, 17.33) * mm, "end": v(-28.69, 20.05) * mm});
            skArc(sketch, "E111.trimOffspring", {"start": v(-33.84, -8.94) * mm, "mid": v(-33.15, -11.24) * mm, "end": v(-32.3, -13.48) * mm});
            skArc(sketch, "E112.trimOffspring", {"start": v(-30.55, -17.08) * mm, "mid": v(-29.31, -19.13) * mm, "end": v(-27.93, -21.1) * mm});
            skArc(sketch, "E113.trimOffspring", {"start": v(-25.34, -24.14) * mm, "mid": v(-23.63, -25.82) * mm, "end": v(-21.8, -27.37) * mm});
            skArc(sketch, "E114.trimOffspring", {"start": v(-18.54, -29.68) * mm, "mid": v(-16.47, -30.88) * mm, "end": v(-14.32, -31.94) * mm});
            skArc(sketch, "E115.trimOffspring", {"start": v(-10.58, -33.36) * mm, "mid": v(-8.27, -34) * mm, "end": v(-5.92, -34.5) * mm});
            skArc(sketch, "E116.trimOffspring", {"start": v(-1.95, -34.95) * mm, "mid": v(0.45, -35) * mm, "end": v(2.84, -34.88) * mm});
            skArc(sketch, "E117.trimOffspring", {"start": v(6.8, -34.33) * mm, "mid": v(9.14, -33.79) * mm, "end": v(11.43, -33.08) * mm});
            skArc(sketch, "E118.trimOffspring", {"start": v(15.13, -31.56) * mm, "mid": v(17.25, -30.45) * mm, "end": v(19.3, -29.2) * mm});
            skArc(sketch, "E119.trimOffspring", {"start": v(22.5, -26.8) * mm, "mid": v(24.28, -25.2) * mm, "end": v(25.95, -23.49) * mm});
            skArc(sketch, "E120.trimOffspring", {"start": v(28.46, -20.37) * mm, "mid": v(29.79, -18.38) * mm, "end": v(30.98, -16.3) * mm});
            skArc(sketch, "E121.trimOffspring", {"start": v(32.63, -12.65) * mm, "mid": v(33.42, -10.4) * mm, "end": v(34.06, -8.08) * mm});
            skArc(sketch, "E122.trimOffspring", {"start": v(34.75, -4.14) * mm, "mid": v(34.96, -1.75) * mm, "end": v(35, 0.64) * mm});
            skArc(sketch, "E123.trimOffspring", {"start": v(34.7, 4.63) * mm, "mid": v(34.3, 7) * mm, "end": v(33.73, 9.33) * mm});
            skArc(sketch, "E124.trimOffspring", {"start": v(32.45, 13.11) * mm, "mid": v(31.48, 15.3) * mm, "end": v(30.35, 17.42) * mm});
            skArc(sketch, "E125.trimOffspring", {"start": v(28.17, 20.77) * mm, "mid": v(26.68, 22.65) * mm, "end": v(25.07, 24.43) * mm});
            skArc(sketch, "E126.trimOffspring", {"start": v(22.12, 27.12) * mm, "mid": v(20.21, 28.58) * mm, "end": v(18.2, 29.9) * mm});
            skArc(sketch, "E127.trimOffspring", {"start": v(14.68, 31.77) * mm, "mid": v(12.47, 32.7) * mm, "end": v(10.2, 33.48) * mm});
            skArc(sketch, "E128.trimOffspring", {"start": v(6.32, 34.43) * mm, "mid": v(3.94, 34.78) * mm, "end": v(1.55, 34.97) * mm});
            skArc(sketch, "E129.trimOffspring", {"start": v(-2.44, 34.91) * mm, "mid": v(-4.83, 34.67) * mm, "end": v(-7.2, 34.25) * mm});
            skArc(sketch, "E130.trimOffspring", {"start": v(-11.05, 33.2) * mm, "mid": v(-13.3, 32.38) * mm, "end": v(-15.48, 31.39) * mm});
            skArc(sketch, "E131.trimOffspring", {"start": v(-18.96, 29.42) * mm, "mid": v(-20.93, 28.05) * mm, "end": v(-22.8, 26.55) * mm});
            skArc(sketch, "E132.trimOffspring", {"start": v(-25.68, 23.78) * mm, "mid": v(-27.25, 21.96) * mm, "end": v(-28.69, 20.05) * mm});
            skArc(sketch, "E133.trimOffspring", {"start": v(-30.79, 16.64) * mm, "mid": v(-31.86, 14.5) * mm, "end": v(-32.77, 12.28) * mm});
            skArc(sketch, "E134.trimOffspring", {"start": v(-33.96, 8.46) * mm, "mid": v(-34.46, 6.12) * mm, "end": v(-34.8, 3.75) * mm});
            skSolve(sketch);
        }
        {
            var Q0;
            Q0=qCreatedBy(makeId("Top.planeOp"),FACE);
            var sketch = newSketch(context, id + "F10", { "sketchPlane" : qUnion([Q0])});
            skArc(sketch, "E135", {"start": v(-25.49, -0.72) * mm, "mid": v(-25.43, -1.93) * mm, "end": v(-25.3, -3.12) * mm});
            skArc(sketch, "E136", {"start": v(-24.87, 5.64) * mm, "mid": v(-22.44, 6.98) * mm, "end": v(-23.68, 9.46) * mm});
            skArc(sketch, "E137.1.0", {"start": v(-25.49, -0.72) * mm, "mid": v(-23.47, 1.18) * mm, "end": v(-25.29, 3.27) * mm});
            skArc(sketch, "E137.2.0", {"start": v(-24.5, -7.04) * mm, "mid": v(-23.03, -4.7) * mm, "end": v(-25.3, -3.12) * mm});
            skArc(sketch, "E137.3.0", {"start": v(-21.99, -12.91) * mm, "mid": v(-21.13, -10.28) * mm, "end": v(-23.74, -9.32) * mm});
            skArc(sketch, "E137.4.0", {"start": v(-18.09, -17.98) * mm, "mid": v(-17.91, -15.2) * mm, "end": v(-20.67, -14.93) * mm});
            skArc(sketch, "E137.5.0", {"start": v(-13.05, -21.9) * mm, "mid": v(-13.57, -19.19) * mm, "end": v(-16.31, -19.6) * mm});
            skArc(sketch, "E137.6.0", {"start": v(-7.19, -24.47) * mm, "mid": v(-8.37, -21.96) * mm, "end": v(-10.92, -23.04) * mm});
            skArc(sketch, "E137.7.0", {"start": v(-0.88, -25.48) * mm, "mid": v(-2.65, -23.35) * mm, "end": v(-4.85, -25.03) * mm});
            skArc(sketch, "E137.8.0", {"start": v(5.49, -24.9) * mm, "mid": v(3.24, -23.28) * mm, "end": v(1.53, -25.45) * mm});
            skArc(sketch, "E137.9.0", {"start": v(11.5, -22.76) * mm, "mid": v(8.93, -21.74) * mm, "end": v(7.81, -24.27) * mm});
            skArc(sketch, "E137.10.0", {"start": v(16.8, -19.18) * mm, "mid": v(14.05, -18.83) * mm, "end": v(13.6, -21.57) * mm});
            skArc(sketch, "E137.11.0", {"start": v(21.05, -14.4) * mm, "mid": v(18.3, -14.75) * mm, "end": v(18.54, -17.5) * mm});
            skArc(sketch, "E137.12.0", {"start": v(23.97, -8.71) * mm, "mid": v(21.39, -9.73) * mm, "end": v(22.31, -12.35) * mm});
            skArc(sketch, "E137.13.0", {"start": v(25.38, -2.48) * mm, "mid": v(23.14, -4.1) * mm, "end": v(24.68, -6.41) * mm});
            skArc(sketch, "E137.14.0", {"start": v(25.2, 3.91) * mm, "mid": v(23.43, 1.77) * mm, "end": v(25.5, -0.07) * mm});
            skArc(sketch, "E137.15.0", {"start": v(23.43, 10.06) * mm, "mid": v(22.26, 7.55) * mm, "end": v(24.72, 6.27) * mm});
            skArc(sketch, "E137.16.0", {"start": v(20.2, 15.57) * mm, "mid": v(19.68, 12.84) * mm, "end": v(22.38, 12.22) * mm});
            skArc(sketch, "E137.17.0", {"start": v(15.7, 20.1) * mm, "mid": v(15.87, 17.33) * mm, "end": v(18.64, 17.4) * mm});
            skArc(sketch, "E137.18.0", {"start": v(10.2, 23.37) * mm, "mid": v(11.06, 20.74) * mm, "end": v(13.73, 21.5) * mm});
            skArc(sketch, "E137.19.0", {"start": v(4.07, 25.17) * mm, "mid": v(5.55, 22.83) * mm, "end": v(7.95, 24.23) * mm});
            skArc(sketch, "E137.20.0", {"start": v(-2.32, 25.4) * mm, "mid": v(-0.3, 23.5) * mm, "end": v(1.67, 25.44) * mm});
            skArc(sketch, "E137.21.0", {"start": v(-8.56, 24.02) * mm, "mid": v(-6.13, 22.69) * mm, "end": v(-4.7, 25.06) * mm});
            skArc(sketch, "E137.22.0", {"start": v(-14.27, 21.13) * mm, "mid": v(-11.58, 20.45) * mm, "end": v(-10.8, 23.1) * mm});
            skArc(sketch, "E137.23.0", {"start": v(-19.08, 16.92) * mm, "mid": v(-16.3, 16.92) * mm, "end": v(-16.2, 19.7) * mm});
            skArc(sketch, "E137.24.0", {"start": v(-22.69, 11.65) * mm, "mid": v(-20, 12.34) * mm, "end": v(-20.59, 15.05) * mm});
            skArc(sketch, "E138.trimOffspring", {"start": v(-24.5, -7.04) * mm, "mid": v(-24.15, -8.19) * mm, "end": v(-23.74, -9.32) * mm});
            skArc(sketch, "E139.trimOffspring", {"start": v(-21.99, -12.91) * mm, "mid": v(-21.35, -13.94) * mm, "end": v(-20.67, -14.93) * mm});
            skArc(sketch, "E140.trimOffspring", {"start": v(-18.09, -17.98) * mm, "mid": v(-17.22, -18.8) * mm, "end": v(-16.31, -19.6) * mm});
            skArc(sketch, "E141.trimOffspring", {"start": v(-13.05, -21.9) * mm, "mid": v(-12, -22.5) * mm, "end": v(-10.92, -23.04) * mm});
            skArc(sketch, "E142.trimOffspring", {"start": v(-7.19, -24.47) * mm, "mid": v(-6.03, -24.78) * mm, "end": v(-4.85, -25.03) * mm});
            skArc(sketch, "E143.trimOffspring", {"start": v(-0.88, -25.48) * mm, "mid": v(0.32, -25.5) * mm, "end": v(1.53, -25.45) * mm});
            skArc(sketch, "E144.trimOffspring", {"start": v(5.49, -24.9) * mm, "mid": v(6.66, -24.62) * mm, "end": v(7.81, -24.27) * mm});
            skArc(sketch, "E145.trimOffspring", {"start": v(11.5, -22.76) * mm, "mid": v(12.57, -22.19) * mm, "end": v(13.6, -21.57) * mm});
            skArc(sketch, "E146.trimOffspring", {"start": v(16.8, -19.18) * mm, "mid": v(17.7, -18.36) * mm, "end": v(18.54, -17.5) * mm});
            skArc(sketch, "E147.trimOffspring", {"start": v(21.05, -14.4) * mm, "mid": v(21.7, -13.39) * mm, "end": v(22.31, -12.35) * mm});
            skArc(sketch, "E148.trimOffspring", {"start": v(23.97, -8.71) * mm, "mid": v(24.35, -7.57) * mm, "end": v(24.68, -6.41) * mm});
            skArc(sketch, "E149.trimOffspring", {"start": v(25.38, -2.48) * mm, "mid": v(25.47, -1.28) * mm, "end": v(25.5, -0.07) * mm});
            skArc(sketch, "E150.trimOffspring", {"start": v(25.2, 3.91) * mm, "mid": v(24.99, 5.1) * mm, "end": v(24.72, 6.27) * mm});
            skArc(sketch, "E151.trimOffspring", {"start": v(23.43, 10.06) * mm, "mid": v(22.93, 11.15) * mm, "end": v(22.38, 12.22) * mm});
            skArc(sketch, "E152.trimOffspring", {"start": v(20.2, 15.57) * mm, "mid": v(19.44, 16.5) * mm, "end": v(18.64, 17.4) * mm});
            skArc(sketch, "E153.trimOffspring", {"start": v(15.7, 20.1) * mm, "mid": v(14.72, 20.82) * mm, "end": v(13.73, 21.5) * mm});
            skArc(sketch, "E154.trimOffspring", {"start": v(10.2, 23.37) * mm, "mid": v(9.08, 23.83) * mm, "end": v(7.95, 24.23) * mm});
            skArc(sketch, "E155.trimOffspring", {"start": v(4.07, 25.17) * mm, "mid": v(2.87, 25.34) * mm, "end": v(1.67, 25.44) * mm});
            skArc(sketch, "E156.trimOffspring", {"start": v(-2.32, 25.4) * mm, "mid": v(-3.52, 25.26) * mm, "end": v(-4.7, 25.06) * mm});
            skArc(sketch, "E157.trimOffspring", {"start": v(-8.56, 24.02) * mm, "mid": v(-9.69, 23.59) * mm, "end": v(-10.8, 23.1) * mm});
            skArc(sketch, "E158.trimOffspring", {"start": v(-14.27, 21.13) * mm, "mid": v(-15.25, 20.44) * mm, "end": v(-16.2, 19.7) * mm});
            skArc(sketch, "E159.trimOffspring", {"start": v(-19.08, 16.92) * mm, "mid": v(-19.85, 16) * mm, "end": v(-20.59, 15.05) * mm});
            skArc(sketch, "E160.trimOffspring", {"start": v(-22.69, 11.65) * mm, "mid": v(-23.2, 10.56) * mm, "end": v(-23.68, 9.46) * mm});
            skArc(sketch, "E161.trimOffspring", {"start": v(-24.87, 5.64) * mm, "mid": v(-25.1, 4.46) * mm, "end": v(-25.29, 3.27) * mm});
            skSolve(sketch);
        }
        {
            var Q0;
            Q0 = qSketchRegion(id + "F10", true);
            var Q1;
            Q1 = qSketchRegion(id + "F9", true);
            var Q2;
            Q2 = qSketchRegion(id + "F8", true);
            var Q3;
            Q3 = qSketchRegion(id + "F7", true);
            var Q4;
            Q4 = qSketchRegion(id + "F6", true);
            var Q5;
            Q5 = qSketchRegion(id + "F5", true);
            loft(context, id + "F11", {"sheetProfilesArray" : [{ "sheetProfileEntities" : qUnion([Q0]) }, { "sheetProfileEntities" : qUnion([Q1]) }, { "sheetProfileEntities" : qUnion([Q2]) }, { "sheetProfileEntities" : qUnion([Q3]) }, { "sheetProfileEntities" : qUnion([Q4]) }, { "sheetProfileEntities" : qUnion([Q5]) }]});
        }
    });
